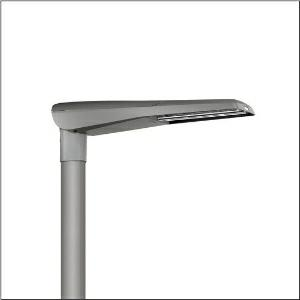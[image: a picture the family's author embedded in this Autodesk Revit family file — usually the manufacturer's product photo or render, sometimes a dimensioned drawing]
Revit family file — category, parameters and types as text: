
# Revit family: streetlight_sl_11_iq_mini___st1_2p1_0_5xc2gc1f08ge_d462
name_source: partatom
category: Lighting Fixtures
units: mm (PartAtom-declared; Revit-internal decimal feet)

## family parameters
Cut with Voids When Loaded = No
Host = Face
Light Source = No
Part Type = Normal
Room Calculation Point = No
Round Connector Dimension = Use Diameter
Shared = No

## types (1)
- --- (1 x LED, 2960 lm, 24.7 W, 2200K)
    Apparent Load = 25 VA
    CIE Flux Codes = 31 68 95 100 100
    Color Rendering = 70
    Color Temperature = 2200K
    Default Elevation = 1800 mm
    Description = Streetlight SL 11 iQ mini, mast luminaire, primary light control with 3 zone facetted reflector, of plastic, silver coated, highly specular, primary optical cover: cover, of PMMA, transparent, light distribution: ST1.2P1.0, light emission: direct distribution, primary light characteristic: asymmetric, installation type: post-top, side-entry, lamps: LED, High Power LED, rated values: 3.480lm | 24,3W | 143,2lm/W (begin service life); end service life: 3.480lm | 25W; at 50% lumin. flux: 1.740lm | 12,5W | 139,2lm/W, colour temperature: 2200/2700/3000/4000K, colour rendering: CRI > 70, light colour: 722/727/730/740, light setting 1 begin service life: 100% | 3.480lm | 24,3W | 143,2lm/W | 3.000K, light setting 1 end service life: 25W, further light settings possible, control: Street-Remote, Auto-Match, Temp-Guard, Lumen-Switch, Night-Set, Smart-Wire, Light-Fading, Desk-Remote (wireless, voltage-free reading and setting of iQ features in the workshop via application-optimized NFC function/RFID function), optimised constant luminous flux control (CLO 2.0), with cable H07RN-F 5x 1.5mm², mains connection: 230..240V, AC, 50/60Hz, connection cable pre-assembled, cable length: 6,5m, luminaire housing, of diecast aluminium, powder-coated, Siteco® metallic grey (DB 702S), please order mast flange separately, inclination adjustable without tools: 0°, 5°, 10°, 15° (post-top) | 0°, -5°, -10°, -15° (side-entry), sealing non-destructively replaceable, multi-level sealing system, length: 736mm, width: 174mm, height: 116mm, mast flange for spigot size: 42mm (side-entry): 5XC10008XM4, 60/48mm (side-entry/post-top): 5XC10108XM2, 76/60mm (side-entry/post-top): 5XC10108XM1, equipment: standard, protection rating (complete): IP66, insulation class (complete): insulation class II (safety insulation), certification: CE, ENEC, ENEC+, VDE, impact resistance: IK10, permissible operating ambient temperature for outdoor applications: -25..+50°C, standard-compliant lighting for roads and squares, Environmental Product Declaration (EPD) tested and certified by an independent institute, packaging unit: 1 piece

Light Distribution: ST1.2P1.0
    Height = 116 mm
    Lamp = 1 x LED
    Lamp Light Flux = 2960 lm
    Lamp Power = 24.7 W
    Lamp count = 1
    Length = 736 mm
    Luminous efficacy = 120 lm/W
    Manufacturer = Siteco
    ModVariant = No
    Model = 5XC2GC1F08GE
    Number of Poles = 1
    OnlyDefault = Yes
    Power Factor = 1
    Product Name = Streetlight SL 11 iQ mini | ST1.2P1.0
    Product group = mast luminaire | pylon top
    ProductGroupID = 6100
    Protection Class = Protection class II
    Protection Degree = IP 66
    RLX_Detail_Level = 1
    RLX_Emergency_Light_Flux = 0 lm
    RLX_Emergency_Type = 0
    RLX_Emergency_Type_DB = No
    RlxData = <blob elided: 53193 chars, md5=4fcb8b01>
    Socket = socket
    Standby Power = 0 W
    System Light Flux = 2960 lm
    System Power = 25 W
    Type Comments = individual setting: luminous flux: 100 % | dim-lin: 254 | 342 mA
    Type Image = l_1003508.jpg
    URL = http://relux.com
    VarID = @adj_034516
    Voltage = 0 V
    Weight = 0.00 kg
    Width = 174 mm

## geometry (parser evidence)
native form markers: Blend x4, Sweep x9
no freeform markers — native parametric forms only
